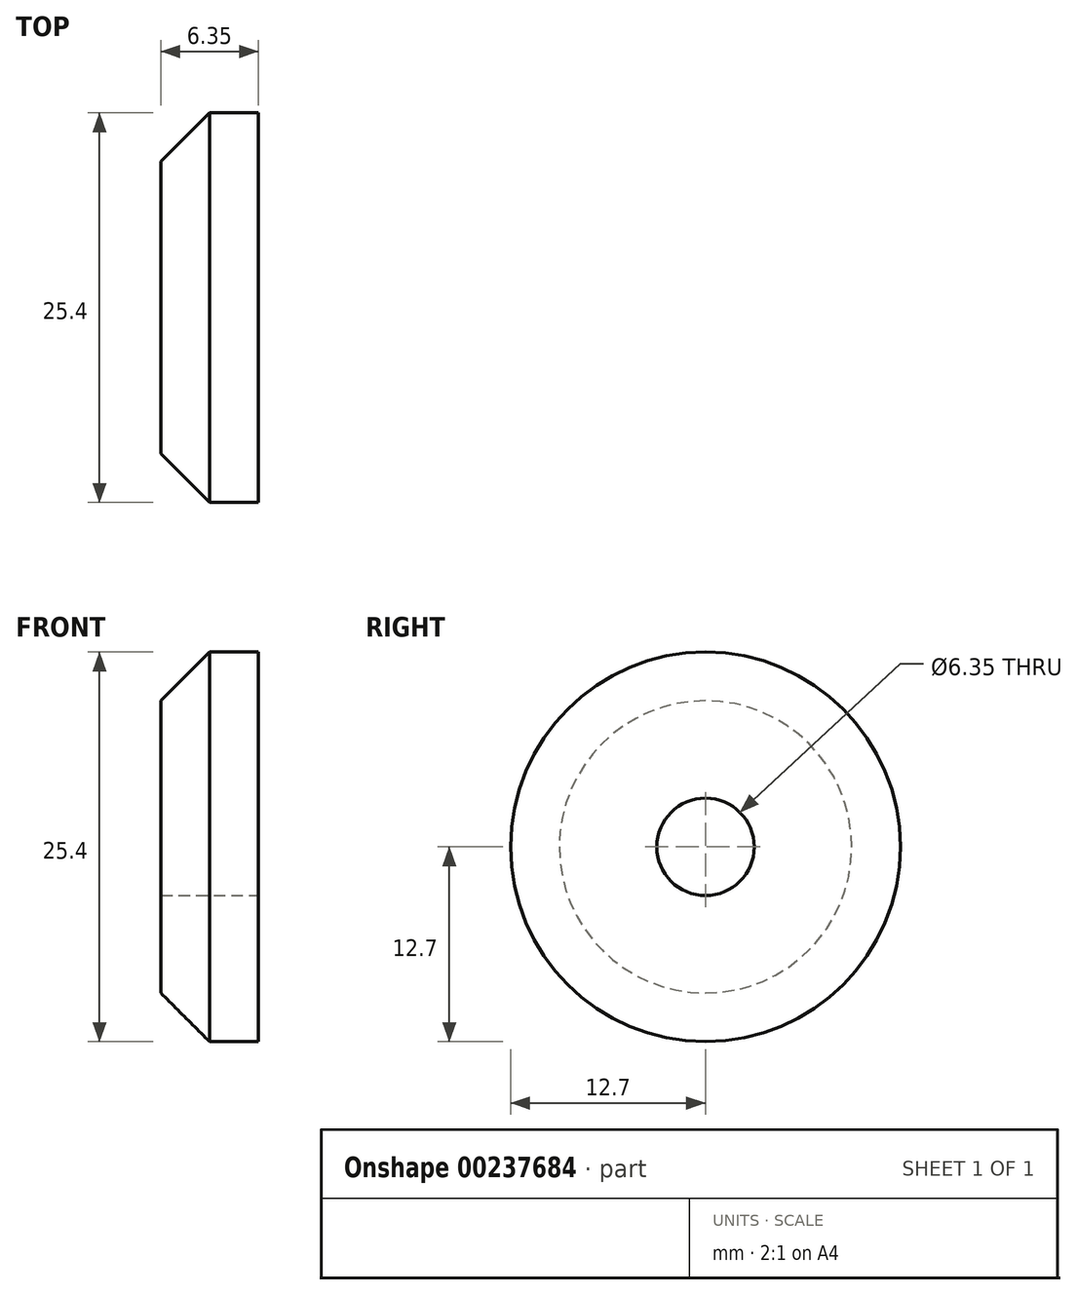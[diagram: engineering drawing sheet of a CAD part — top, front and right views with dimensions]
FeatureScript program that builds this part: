
annotation { "Feature Type Name" : "Feature", "Feature Type Description" : "" }
export const myFeature = defineFeature(function(context is Context, id is Id, definition is map)
    precondition{}
    {
        {
            var Q0;
            Q0=qCreatedBy(makeId("Right.planeOp"),FACE);
            var sketch = newSketch(context, id + "F0", { "sketchPlane" : qUnion([Q0])});
            skCircle(sketch, "E0", {"center": v(0, 0) * mm, "radius": 12.7 * mm});
            skSolve(sketch);
        }
        {
            var Q0;
            Q0 = qSketchRegion(id + "F0", true);
            extrude(context, id + "F1", {"entities" : qUnion([Q0]), "oppositeDirection" : true, "depth" : 6.35 * mm});
        }
        {
            var Q0;
            Q0=makeQuery(id+"F1.opExtrude","CAP_FACE",FACE,{"disambiguationData":[OSD([sQuery(id+"F0.wireOp",EDGE,"E0")])],"isStart":true});
            var sketch = newSketch(context, id + "F2", { "sketchPlane" : qUnion([Q0])});
            skPoint(sketch, "E1", {"position": v(0, 0) * mm});
            skSolve(sketch);
        }
        {
            var Q0;
            Q0=sQuery(id+"F2.wireOp",VERTEX,"E1");
            var Q1;
            Q1=makeQuery(id+"F1.opExtrude","SWEPT_BODY",BODY,{"disambiguationData":[OSD([sQuery(id+"F0.wireOp",EDGE,"E0")])]});
            hole(context, id + "F3", {"style" : HoleStyle.SIMPLE, "endStyle" : HoleEndStyle.THROUGH, "holeDiameter" : 6.35 * mm, "locations" : qUnion([Q0]), "scope" : qUnion([Q1]), "isTappedThrough" : true});
        }
        {
            var Q0;
            Q0=makeQuery(id+"F1.opExtrude","CAP_EDGE",EDGE,{"disambiguationData":[OSD([sQuery(id+"F0.wireOp",EDGE,"E0")])],"isStart":false});
            chamfer(context, id + "F4", {"entities" : qUnion([Q0]), "width" : 3.17 * mm, "tangentPropagation" : true});
        }
    });
